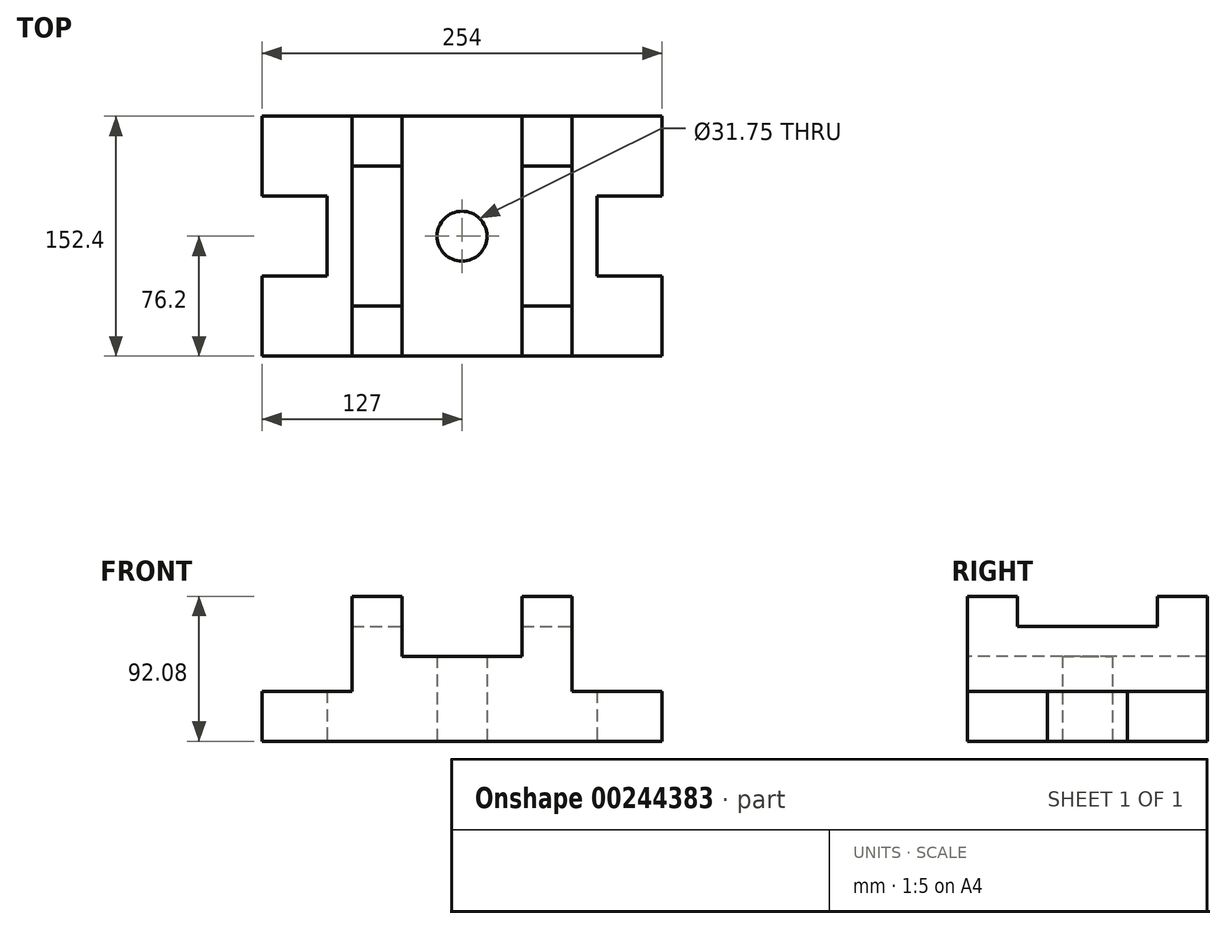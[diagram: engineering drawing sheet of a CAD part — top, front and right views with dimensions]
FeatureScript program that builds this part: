
annotation { "Feature Type Name" : "Feature", "Feature Type Description" : "" }
export const myFeature = defineFeature(function(context is Context, id is Id, definition is map)
    precondition{}
    {
        {
            var Q0;
            Q0=qCreatedBy(makeId("Top.planeOp"),FACE);
            var sketch = newSketch(context, id + "F0", { "sketchPlane" : qUnion([Q0])});
            skLineSegment(sketch, "E0", {"start": v(0, 0) * mm, "end": v(-254, 0) * mm});
            skLineSegment(sketch, "E1", {"start": v(-254, 0) * mm, "end": v(-254, 50.8) * mm});
            skLineSegment(sketch, "E2", {"start": v(-254, 152.4) * mm, "end": v(0, 152.4) * mm});
            skLineSegment(sketch, "E3", {"start": v(0, 152.4) * mm, "end": v(0, 101.6) * mm});
            skLineSegment(sketch, "E4", {"start": v(-254, 101.6) * mm, "end": v(-212.72, 101.6) * mm});
            skLineSegment(sketch, "E5", {"start": v(-212.72, 101.6) * mm, "end": v(-212.72, 50.8) * mm});
            skLineSegment(sketch, "E6", {"start": v(-212.72, 50.8) * mm, "end": v(-254, 50.8) * mm});
            skLineSegment(sketch, "E7", {"start": v(0, 101.6) * mm, "end": v(-41.27, 101.6) * mm});
            skLineSegment(sketch, "E8", {"start": v(-41.27, 101.6) * mm, "end": v(-41.27, 50.8) * mm});
            skLineSegment(sketch, "E9", {"start": v(-41.27, 50.8) * mm, "end": v(0, 50.8) * mm});
            skLineSegment(sketch, "E10", {"start": v(0, 50.8) * mm, "end": v(0, 0) * mm});
            skLineSegment(sketch, "E11.trimOffspring", {"start": v(-254, 101.6) * mm, "end": v(-254, 152.4) * mm});
            skLineSegment(sketch, "E12", {"start": v(-127, 0) * mm, "end": v(-127, 76.2) * mm, "construction": true});
            skCircle(sketch, "E13", {"center": v(-127, 76.2) * mm, "radius": 15.88 * mm});
            skSolve(sketch);
        }
        {
            var Q0;
            Q0 = qSketchRegion(id + "F0", true);
            var Q1;
            Q1=makeQuery(id+"F0.imprint","IMPRINT",FACE,{"disambiguationData":[TD([[makeQuery(id+"F0.imprint","IMPRINT",EDGE,{"derivedFrom":sQuery(id+"F0.wireOp",EDGE,"E0")}),-1.0]])]});
            extrude(context, id + "F1", {"entities" : qUnion([Q0, Q1]), "depth" : 31.75 * mm});
        }
        {
            var Q0;
            Q0=makeQuery(id+"F1.opExtrude","CAP_FACE",FACE,{"disambiguationData":[OSD([sQuery(id+"F0.wireOp",EDGE,"E0"),sQuery(id+"F0.wireOp",EDGE,"E2"),sQuery(id+"F0.wireOp",EDGE,"E3"),sQuery(id+"F0.wireOp",EDGE,"E4"),sQuery(id+"F0.wireOp",EDGE,"E5"),sQuery(id+"F0.wireOp",EDGE,"E6"),sQuery(id+"F0.wireOp",EDGE,"E7"),sQuery(id+"F0.wireOp",EDGE,"E8"),sQuery(id+"F0.wireOp",EDGE,"E9"),sQuery(id+"F0.wireOp",EDGE,"IlmANAsM-MZeF-u2fV-SS2p-bOOOLUpDbYE7"),sQuery(id+"F0.wireOp",EDGE,"E11.trimOffspring"),sQuery(id+"F0.wireOp",EDGE,"c29a67ac-a2b6-4afc-b0a5-bde3154c6ccb.trimOffspring")])],"isStart":false});
            var sketch = newSketch(context, id + "F2", { "sketchPlane" : qUnion([Q0])});
            skLineSegment(sketch, "E14", {"start": v(-196.85, 152.4) * mm, "end": v(-196.85, 0) * mm});
            skLineSegment(sketch, "E15", {"start": v(-57.15, 152.4) * mm, "end": v(-57.15, 0) * mm});
            skLineSegment(sketch, "E16", {"start": v(-127, 0) * mm, "end": v(-127, 76.2) * mm, "construction": true});
            skCircle(sketch, "E17", {"center": v(-127, 76.2) * mm, "radius": 15.88 * mm});
            skLineSegment(sketch, "E18", {"start": v(-196.85, 128.25) * mm, "end": v(-254, 128.25) * mm, "construction": true});
            skLineSegment(sketch, "E19", {"start": v(-57.15, 127.48) * mm, "end": v(0, 127.48) * mm, "construction": true});
            skSolve(sketch);
        }
        {
            var Q0;
            {var subQ0=sQuery(id+"F2.wireOp",EDGE,"E14");Q0=makeQuery(id+"F2.imprint","IMPRINT",FACE,{"disambiguationData":[TD([[makeQuery(id+"F2.imprint","IMPRINT",EDGE,{"derivedFrom":subQ0}),1.0]])]});}
            extrude(context, id + "F3", {"entities" : qUnion([Q0]), "operationType" : NewBodyOperationType.ADD, "depth" : 22.22 * mm});
        }
        {
            var Q0;
            Q0=makeQuery(id+"F3.opExtrude","CAP_FACE",FACE,{"disambiguationData":[OSD([sQuery(id+"F0.wireOp",EDGE,"E0"),sQuery(id+"F0.wireOp",EDGE,"E2"),sQuery(id+"F2.wireOp",EDGE,"E14"),sQuery(id+"F2.wireOp",EDGE,"E15")])],"isStart":false});
            var sketch = newSketch(context, id + "F4", { "sketchPlane" : qUnion([Q0])});
            skLineSegment(sketch, "E20", {"start": v(-165.1, 152.4) * mm, "end": v(-165.1, 0) * mm});
            skLineSegment(sketch, "E21", {"start": v(-88.9, 152.4) * mm, "end": v(-88.9, 0) * mm});
            skLineSegment(sketch, "E22", {"start": v(-196.85, 122.34) * mm, "end": v(-165.1, 122.34) * mm, "construction": true});
            skLineSegment(sketch, "E23", {"start": v(-88.9, 125.3) * mm, "end": v(-57.15, 125.3) * mm, "construction": true});
            skSolve(sketch);
        }
        {
            var Q0;
            Q0 = qSketchRegion(id + "F4", true);
            var Q1;
            {var subQ0=sQuery(id+"F4.wireOp",EDGE,"E20");Q1=makeQuery(id+"F4.imprint","IMPRINT",FACE,{"disambiguationData":[TD([[makeQuery(id+"F4.imprint","IMPRINT",EDGE,{"derivedFrom":subQ0}),-1.0]])]});}
            extrude(context, id + "F5", {"entities" : qUnion([Q0, Q1]), "operationType" : NewBodyOperationType.ADD, "depth" : 19.05 * mm});
        }
        {
            var Q0;
            {var subQ0=sQuery(id+"F4.wireOp",EDGE,"E21");Q0=makeQuery(id+"F4.imprint","IMPRINT",FACE,{"disambiguationData":[TD([[makeQuery(id+"F4.imprint","IMPRINT",EDGE,{"derivedFrom":subQ0}),1.0]])]});}
            extrude(context, id + "F6", {"entities" : qUnion([Q0]), "operationType" : NewBodyOperationType.ADD, "depth" : 19.05 * mm});
        }
        {
            var Q0;
            Q0=makeQuery(id+"F5.opExtrude","CAP_FACE",FACE,{"disambiguationData":[OSD([sQuery(id+"F0.wireOp",EDGE,"E0"),sQuery(id+"F0.wireOp",EDGE,"E2"),sQuery(id+"F2.wireOp",EDGE,"E14"),sQuery(id+"F4.wireOp",EDGE,"E20")])],"isStart":false});
            var sketch = newSketch(context, id + "F7", { "sketchPlane" : qUnion([Q0])});
            skLineSegment(sketch, "E24", {"start": v(-196.85, 120.65) * mm, "end": v(-165.1, 120.65) * mm});
            skLineSegment(sketch, "E25", {"start": v(-196.85, 31.75) * mm, "end": v(-165.1, 31.75) * mm});
            skLineSegment(sketch, "E26", {"start": v(-185.6, 152.4) * mm, "end": v(-185.6, 120.65) * mm, "construction": true});
            skLineSegment(sketch, "E27", {"start": v(-183.7, 31.75) * mm, "end": v(-183.7, 0) * mm, "construction": true});
            skPoint(sketch, "E27.endSnap0", {"position": v(-180.97, 0) * mm});
            skSolve(sketch);
        }
        {
            var Q0;
            {var subQ0=sQuery(id+"F7.wireOp",EDGE,"E24");Q0=makeQuery(id+"F7.imprint","IMPRINT",FACE,{"disambiguationData":[TD([[makeQuery(id+"F7.imprint","IMPRINT",EDGE,{"derivedFrom":subQ0}),1.0]])]});}
            extrude(context, id + "F8", {"entities" : qUnion([Q0]), "operationType" : NewBodyOperationType.ADD, "depth" : 19.05 * mm});
        }
        {
            var Q0;
            {var subQ0=sQuery(id+"F7.wireOp",EDGE,"E25");Q0=makeQuery(id+"F7.imprint","IMPRINT",FACE,{"disambiguationData":[TD([[makeQuery(id+"F7.imprint","IMPRINT",EDGE,{"derivedFrom":subQ0}),-1.0]])]});}
            extrude(context, id + "F9", {"entities" : qUnion([Q0]), "operationType" : NewBodyOperationType.ADD, "depth" : 19.05 * mm});
        }
        {
            var Q0;
            Q0=makeQuery(id+"F6.opExtrude","CAP_FACE",FACE,{"disambiguationData":[OSD([sQuery(id+"F0.wireOp",EDGE,"E0"),sQuery(id+"F0.wireOp",EDGE,"E2"),sQuery(id+"F2.wireOp",EDGE,"E15"),sQuery(id+"F4.wireOp",EDGE,"E21")])],"isStart":false});
            var sketch = newSketch(context, id + "F10", { "sketchPlane" : qUnion([Q0])});
            skLineSegment(sketch, "E28", {"start": v(-88.9, 120.65) * mm, "end": v(-57.15, 120.65) * mm});
            skLineSegment(sketch, "E29", {"start": v(-88.9, 31.75) * mm, "end": v(-57.15, 31.75) * mm});
            skLineSegment(sketch, "E30", {"start": v(-85.1, 152.4) * mm, "end": v(-85.1, 120.65) * mm, "construction": true});
            skPoint(sketch, "E30.endSnap0", {"position": v(-73.03, 120.65) * mm});
            skLineSegment(sketch, "E31", {"start": v(-86.62, 31.75) * mm, "end": v(-86.62, 0) * mm, "construction": true});
            skSolve(sketch);
        }
        {
            var Q0;
            {var subQ0=sQuery(id+"F10.wireOp",EDGE,"E28");Q0=makeQuery(id+"F10.imprint","IMPRINT",FACE,{"disambiguationData":[TD([[makeQuery(id+"F10.imprint","IMPRINT",EDGE,{"derivedFrom":subQ0}),1.0]])]});}
            extrude(context, id + "F11", {"entities" : qUnion([Q0]), "operationType" : NewBodyOperationType.ADD, "depth" : 19.05 * mm});
        }
        {
            var Q0;
            {var subQ0=sQuery(id+"F10.wireOp",EDGE,"E29");Q0=makeQuery(id+"F10.imprint","IMPRINT",FACE,{"disambiguationData":[TD([[makeQuery(id+"F10.imprint","IMPRINT",EDGE,{"derivedFrom":subQ0}),-1.0]])]});}
            extrude(context, id + "F12", {"entities" : qUnion([Q0]), "operationType" : NewBodyOperationType.ADD, "depth" : 19.05 * mm});
        }
    });
